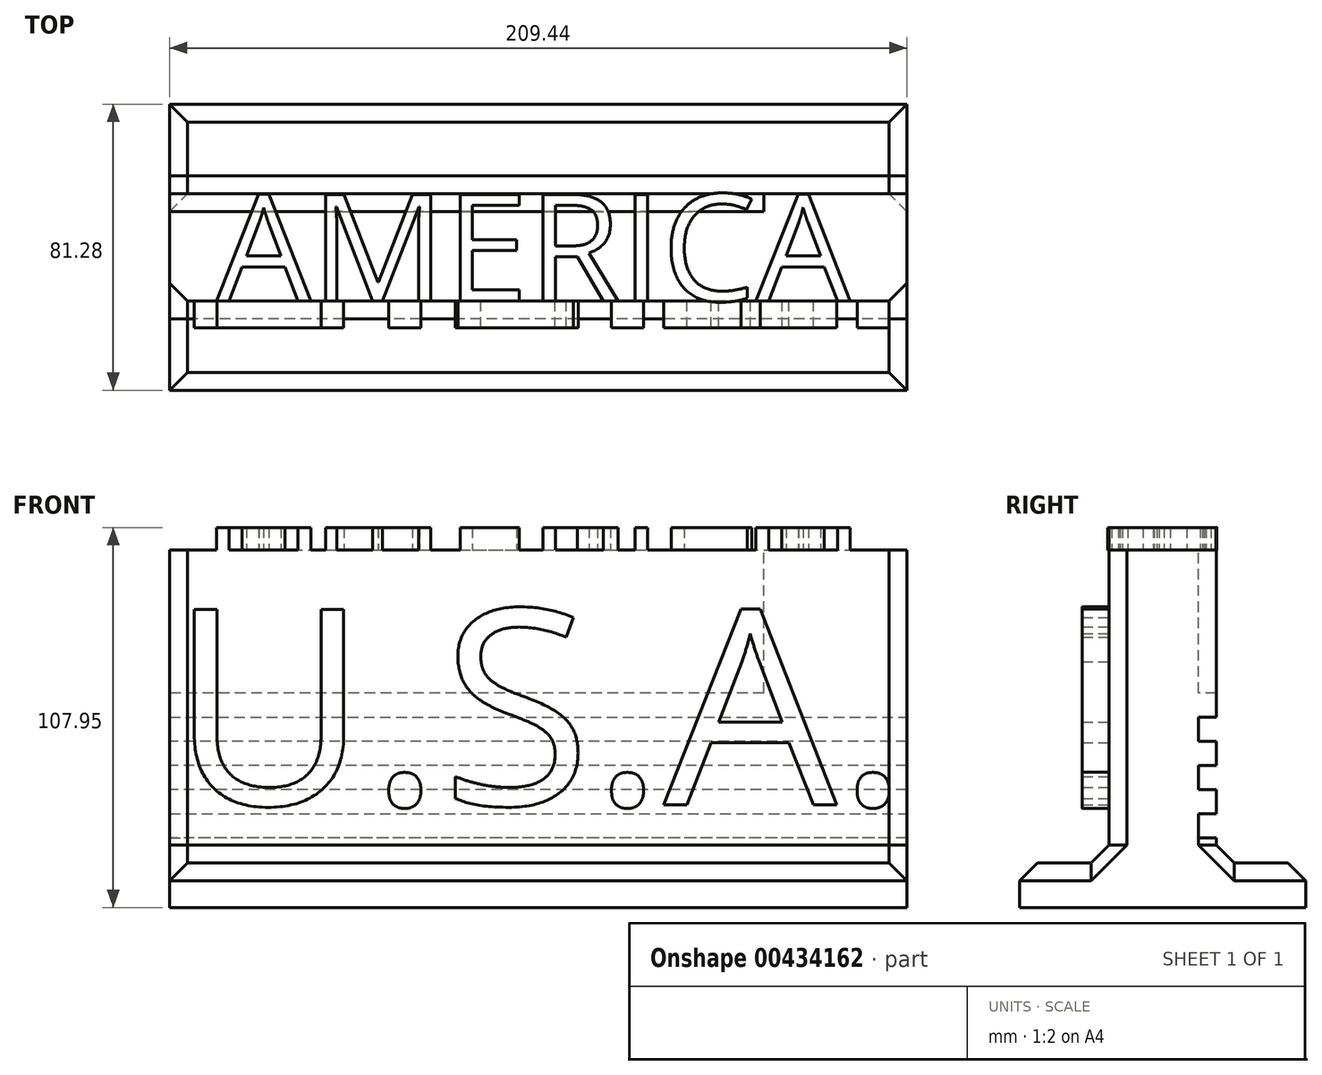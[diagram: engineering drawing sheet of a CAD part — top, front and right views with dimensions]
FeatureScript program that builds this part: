
annotation { "Feature Type Name" : "Feature", "Feature Type Description" : "" }
export const myFeature = defineFeature(function(context is Context, id is Id, definition is map)
    precondition{}
    {
        {
            var Q0;
            Q0=qCreatedBy(makeId("Front.planeOp"),FACE);
            var sketch = newSketch(context, id + "F0", { "sketchPlane" : qUnion([Q0])});
            skLineSegment(sketch, "E0.bottom", {"start": v(-72.19, -36.87) * mm, "end": v(137.25, -36.87) * mm});
            skLineSegment(sketch, "E0.top", {"start": v(-72.19, 52.03) * mm, "end": v(137.25, 52.03) * mm});
            skLineSegment(sketch, "E0.left", {"start": v(-72.19, -36.87) * mm, "end": v(-72.19, 52.03) * mm});
            skLineSegment(sketch, "E0.right", {"start": v(137.25, -36.87) * mm, "end": v(137.25, 52.03) * mm});
            skLineSegment(sketch, "E1", {"start": v(-72.19, -36.87) * mm, "end": v(-72.19, -20.36) * mm});
            skLineSegment(sketch, "E2", {"start": v(137.25, 52.03) * mm, "end": v(137.25, 35.52) * mm});
            skSolve(sketch);
        }
        {
            var Q0;
            Q0 = qSketchRegion(id + "F0", true);
            extrude(context, id + "F1", {"entities" : qUnion([Q0]), "depth" : 25.4 * mm, "offsetDistance" : 25.4 * mm});
        }
        {
            var Q0;
            Q0=makeQuery(id+"F1.opExtrude","CAP_FACE",FACE,{"disambiguationData":[OSD([sQuery(id+"F0.wireOp",EDGE,"E0.bottom"),sQuery(id+"F0.wireOp",EDGE,"E0.top"),sQuery(id+"F0.wireOp",EDGE,"E0.left"),sQuery(id+"F0.wireOp",EDGE,"E0.right"),sQuery(id+"F0.wireOp",EDGE,"E1"),sQuery(id+"F0.wireOp",EDGE,"E2")])],"isStart":false});
            var sketch = newSketch(context, id + "F2", { "sketchPlane" : qUnion([Q0])});
            skLineSegment(sketch, "E3", {"start": v(-72.19, -36.87) * mm, "end": v(-72.19, -20.36) * mm});
            skLineSegment(sketch, "E4", {"start": v(137.25, 52.03) * mm, "end": v(137.25, 35.52) * mm});
            skText(sketch, "E5", { "text": "U.S.A.", "fontName": "OpenSans-Regular.ttf"});
            const initialGuessF2  = {"E5": [-0.07219, -0.02036, 1, 0, 0.05588]};
            skSetInitialGuess(sketch, initialGuessF2);
            skSolve(sketch);
        }
        {
            var Q0;
            Q0 = qSketchRegion(id + "F2", true);
            extrude(context, id + "F3", {"entities" : qUnion([Q0]), "operationType" : NewBodyOperationType.ADD, "depth" : 7.62 * mm, "offsetDistance" : 25.4 * mm});
        }
        {
            var Q0;
            Q0=makeQuery(id+"F1.opExtrude","CAP_FACE",FACE,{"disambiguationData":[OSD([sQuery(id+"F0.wireOp",EDGE,"E0.bottom"),sQuery(id+"F0.wireOp",EDGE,"E0.top"),sQuery(id+"F0.wireOp",EDGE,"E0.left"),sQuery(id+"F0.wireOp",EDGE,"E0.right"),sQuery(id+"F0.wireOp",EDGE,"E1"),sQuery(id+"F0.wireOp",EDGE,"E2")])],"isStart":true});
            var sketch = newSketch(context, id + "F4", { "sketchPlane" : qUnion([Q0])});
            skLineSegment(sketch, "E6", {"start": v(-137.25, 52.03) * mm, "end": v(-137.25, 11.39) * mm});
            skLineSegment(sketch, "E7", {"start": v(-137.25, 11.39) * mm, "end": v(-96.61, 11.39) * mm});
            skLineSegment(sketch, "E8", {"start": v(-96.61, 11.39) * mm, "end": v(-96.61, 52.03) * mm});
            skLineSegment(sketch, "E9", {"start": v(-96.61, 52.03) * mm, "end": v(-137.25, 52.03) * mm});
            skLineSegment(sketch, "E10", {"start": v(-96.61, 52.03) * mm, "end": v(-96.61, 45.17) * mm});
            skLineSegment(sketch, "E11", {"start": v(-96.61, 45.17) * mm, "end": v(-96.61, 38.31) * mm});
            skLineSegment(sketch, "E12", {"start": v(-96.61, 38.31) * mm, "end": v(-96.61, 31.45) * mm});
            skLineSegment(sketch, "E13", {"start": v(-96.61, 31.45) * mm, "end": v(-96.61, 24.6) * mm});
            skLineSegment(sketch, "E14", {"start": v(-96.61, 24.6) * mm, "end": v(-96.61, 17.74) * mm});
            skLineSegment(sketch, "E15", {"start": v(-96.61, 17.74) * mm, "end": v(-96.61, 11.39) * mm});
            skLineSegment(sketch, "E16", {"start": v(-96.61, -29.76) * mm, "end": v(72.19, -29.76) * mm});
            skLineSegment(sketch, "E17", {"start": v(-96.61, -22.9) * mm, "end": v(72.19, -22.9) * mm});
            skLineSegment(sketch, "E18", {"start": v(-96.61, -16.04) * mm, "end": v(72.19, -16.04) * mm});
            skLineSegment(sketch, "E19", {"start": v(-96.61, -9.19) * mm, "end": v(72.19, -9.19) * mm});
            skLineSegment(sketch, "E20", {"start": v(-96.61, -2.33) * mm, "end": v(72.19, -2.33) * mm});
            skLineSegment(sketch, "E21", {"start": v(-96.61, 4.53) * mm, "end": v(72.19, 4.53) * mm});
            skLineSegment(sketch, "E22", {"start": v(-96.61, 11.39) * mm, "end": v(72.19, 11.39) * mm});
            skLineSegment(sketch, "E23", {"start": v(-96.61, 17.74) * mm, "end": v(72.19, 17.74) * mm});
            skLineSegment(sketch, "E24", {"start": v(-96.61, 24.6) * mm, "end": v(72.19, 24.6) * mm});
            skLineSegment(sketch, "E25", {"start": v(72.19, 31.45) * mm, "end": v(-96.61, 31.45) * mm});
            skLineSegment(sketch, "E26", {"start": v(-96.61, 38.31) * mm, "end": v(72.19, 38.31) * mm});
            skLineSegment(sketch, "E27", {"start": v(-96.61, 45.17) * mm, "end": v(72.19, 45.17) * mm});
            skLineSegment(sketch, "E28", {"start": v(-96.61, 4.53) * mm, "end": v(-137.25, 4.53) * mm});
            skLineSegment(sketch, "E29", {"start": v(-96.61, -2.33) * mm, "end": v(-137.25, -2.33) * mm});
            skLineSegment(sketch, "E30", {"start": v(-137.25, -9.19) * mm, "end": v(-96.61, -9.19) * mm});
            skLineSegment(sketch, "E31", {"start": v(-137.25, -16.04) * mm, "end": v(-96.61, -16.04) * mm});
            skLineSegment(sketch, "E32", {"start": v(-96.61, -22.9) * mm, "end": v(-137.25, -22.9) * mm});
            skLineSegment(sketch, "E33", {"start": v(-96.61, -29.76) * mm, "end": v(-137.25, -29.76) * mm});
            skPoint(sketch, "E34.end.orphan", {"position": v(-96.61, -36.87) * mm});
            skSolve(sketch);
        }
        {
            var Q0;
            Q0=makeQuery(id+"F4.imprint","IMPRINT",FACE,{"disambiguationData":[TD([[makeQuery(id+"F4.imprint","IMPRINT",EDGE,{"derivedFrom":sQuery(id+"F4.wireOp",EDGE,"E6")}),-1.0]])]});
            var Q1;
            Q1=makeQuery(id+"F4.imprint","IMPRINT",FACE,{"disambiguationData":[TD([[makeQuery(id+"F4.imprint","IMPRINT",EDGE,{"derivedFrom":sQuery(id+"F4.wireOp",EDGE,"E12")}),1.0]])]});
            var Q2;
            Q2=makeQuery(id+"F4.imprint","IMPRINT",FACE,{"disambiguationData":[TD([[makeQuery(id+"F4.imprint","IMPRINT",EDGE,{"derivedFrom":sQuery(id+"F4.wireOp",EDGE,"E14")}),1.0]])]});
            var Q3;
            {var subQ0=sQuery(id+"F4.wireOp",EDGE,"E10");Q3=makeQuery(id+"F4.imprint","IMPRINT",FACE,{"disambiguationData":[TD([[makeQuery(id+"F4.imprint","IMPRINT",EDGE,{"derivedFrom":subQ0}),1.0]])]});}
            var Q4;
            {var subQ4=sQuery(id+"F4.wireOp",EDGE,"E7");Q4=makeQuery(id+"F4.imprint","IMPRINT",FACE,{"disambiguationData":[TD([[makeQuery(id+"F4.imprint","IMPRINT",EDGE,{"derivedFrom":subQ4}),-1.0]])]});}
            var Q5;
            {var subQ1=sQuery(id+"F4.wireOp",EDGE,"E19");Q5=makeQuery(id+"F4.imprint","IMPRINT",FACE,{"disambiguationData":[TD([[makeQuery(id+"F4.imprint","IMPRINT",EDGE,{"derivedFrom":subQ1}),1.0]])]});}
            var Q6;
            {var subQ4=sQuery(id+"F4.wireOp",EDGE,"E17");Q6=makeQuery(id+"F4.imprint","IMPRINT",FACE,{"disambiguationData":[TD([[makeQuery(id+"F4.imprint","IMPRINT",EDGE,{"derivedFrom":subQ4}),1.0]])]});}
            var Q7;
            {var subQ3=sQuery(id+"F4.wireOp",EDGE,"E16");Q7=makeQuery(id+"F4.imprint","IMPRINT",FACE,{"disambiguationData":[TD([[makeQuery(id+"F4.imprint","IMPRINT",EDGE,{"derivedFrom":subQ3}),-1.0]])]});}
            extrude(context, id + "F5", {"entities" : qUnion([Q0, Q1, Q2, Q3, Q4, Q5, Q6, Q7]), "operationType" : NewBodyOperationType.ADD, "depth" : 5.08 * mm, "offsetDistance" : 25.4 * mm});
        }
        {
            var Q0;
            {var subQ0=sQuery(id+"F0.wireOp",EDGE,"E0.top");Q0=makeQuery(id+"F5.boolean.opBoolean","MERGE",FACE,{"derivedFrom":[makeQuery(id+"F1.opExtrude","SWEPT_FACE",FACE,{"disambiguationData":[OSD([subQ0])]}),makeQuery(id+"F5.opExtrude","SWEPT_FACE",FACE,{"disambiguationData":[OSD([subQ0,sQuery(id+"F4.wireOp",EDGE,"E9")])]})]});}
            var sketch = newSketch(context, id + "F6", { "sketchPlane" : qUnion([Q0])});
            skLineSegment(sketch, "E35", {"start": v(-72.19, 5.08) * mm, "end": v(-58.85, 5.08) * mm});
            skLineSegment(sketch, "E36", {"start": v(137.25, -25.4) * mm, "end": v(123.9, -25.4) * mm});
            skText(sketch, "E37", { "text": "AMERICA", "fontName": "OpenSans-Regular.ttf"});
            const initialGuessF6  = {"E37": [-0.05885, -0.0254, 1, 0, 0.03048]};
            skSetInitialGuess(sketch, initialGuessF6);
            skSolve(sketch);
        }
        {
            var Q0;
            Q0 = qSketchRegion(id + "F6", true);
            extrude(context, id + "F7", {"entities" : qUnion([Q0]), "operationType" : NewBodyOperationType.ADD, "depth" : 6.35 * mm, "offsetDistance" : 25.4 * mm});
        }
        {
            var Q0;
            {var subQ0=sQuery(id+"F0.wireOp",EDGE,"E0.bottom");Q0=makeQuery(id+"F5.boolean.opBoolean","MERGE",FACE,{"derivedFrom":[makeQuery(id+"F1.opExtrude","SWEPT_FACE",FACE,{"disambiguationData":[OSD([subQ0])]}),makeQuery(id+"F5.opExtrude","SWEPT_FACE",FACE,{"disambiguationData":[OSD([subQ0])]})]});}
            var sketch = newSketch(context, id + "F8", { "sketchPlane" : qUnion([Q0])});
            skLineSegment(sketch, "E38.bottom", {"start": v(-72.19, 25.4) * mm, "end": v(137.25, 25.4) * mm});
            skLineSegment(sketch, "E38.top", {"start": v(-72.19, -5.08) * mm, "end": v(137.25, -5.08) * mm});
            skLineSegment(sketch, "E38.left", {"start": v(-72.19, 25.4) * mm, "end": v(-72.19, -5.08) * mm});
            skLineSegment(sketch, "E38.right", {"start": v(137.25, 25.4) * mm, "end": v(137.25, -5.08) * mm});
            skPoint(sketch, "E39.right.end.orphan", {"position": v(-72.19, 33.56) * mm});
            skLineSegment(sketch, "E40.top", {"start": v(-72.19, 50.8) * mm, "end": v(137.25, 50.8) * mm});
            skLineSegment(sketch, "E40.left", {"start": v(-72.19, 25.4) * mm, "end": v(-72.19, 50.8) * mm});
            skLineSegment(sketch, "E40.right", {"start": v(137.25, 25.4) * mm, "end": v(137.25, 50.8) * mm});
            skLineSegment(sketch, "E41.top", {"start": v(-72.19, -30.48) * mm, "end": v(137.25, -30.48) * mm});
            skLineSegment(sketch, "E41.left", {"start": v(-72.19, -5.08) * mm, "end": v(-72.19, -30.48) * mm});
            skLineSegment(sketch, "E41.right", {"start": v(137.25, -5.08) * mm, "end": v(137.25, -30.48) * mm});
            skSolve(sketch);
        }
        {
            var Q0;
            Q0 = qSketchRegion(id + "F8", true);
            extrude(context, id + "F9", {"entities" : qUnion([Q0]), "operationType" : NewBodyOperationType.ADD, "depth" : 12.7 * mm, "offsetDistance" : 25.4 * mm});
        }
        {
            var Q0;
            {var subQ3=sQuery(id+"F8.wireOp",EDGE,"E41.right");var subQ4=sQuery(id+"F8.wireOp",EDGE,"E40.right");var subQ5=sQuery(id+"F8.wireOp",EDGE,"E38.right");var subQ6=sQuery(id+"F8.wireOp",EDGE,"E41.left");var subQ7=sQuery(id+"F8.wireOp",EDGE,"E40.left");var subQ8=sQuery(id+"F8.wireOp",EDGE,"E38.left");var subQ15=sQuery(id+"F8.wireOp",EDGE,"E41.top");Q0=makeQuery(id+"F9.boolean.opBoolean","SPLIT",FACE,{"disambiguationData":[TD([makeQuery(id+"F9.opExtrude","SWEPT_FACE",FACE,{"disambiguationData":[OSD([subQ15])]})])],"derivedFrom":makeQuery(id+"F9.opExtrude","CAP_FACE",FACE,{"disambiguationData":[OSD([subQ8,subQ5,sQuery(id+"F8.wireOp",EDGE,"E40.top"),subQ7,subQ4,subQ15,subQ6,subQ3])],"isStart":true})});}
            chamfer(context, id + "F10", {"entities" : qUnion([Q0]), "width" : 5.08 * mm, "tangentPropagation" : true});
        }
        {
            var Q0;
            {var subQ7=sQuery(id+"F8.wireOp",EDGE,"E41.right");var subQ8=sQuery(id+"F8.wireOp",EDGE,"E40.right");var subQ9=sQuery(id+"F8.wireOp",EDGE,"E38.right");var subQ12=sQuery(id+"F8.wireOp",EDGE,"E41.left");var subQ13=sQuery(id+"F8.wireOp",EDGE,"E40.left");var subQ14=sQuery(id+"F8.wireOp",EDGE,"E38.left");var subQ15=sQuery(id+"F8.wireOp",EDGE,"E40.top");Q0=makeQuery(id+"F9.boolean.opBoolean","SPLIT",FACE,{"disambiguationData":[TD([makeQuery(id+"F7.opExtrude","SWEPT_FACE",FACE,{"disambiguationData":[OSD([sQuery(id+"F6.wireOp",EDGE,"E37.sketch_text.stroke-3")])]})])],"derivedFrom":makeQuery(id+"F9.opExtrude","CAP_FACE",FACE,{"disambiguationData":[OSD([subQ14,subQ9,subQ15,subQ13,subQ8,sQuery(id+"F8.wireOp",EDGE,"E41.top"),subQ12,subQ7])],"isStart":true})});}
            chamfer(context, id + "F11", {"entities" : qUnion([Q0]), "width" : 5.08 * mm, "tangentPropagation" : true});
        }
    });
